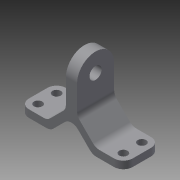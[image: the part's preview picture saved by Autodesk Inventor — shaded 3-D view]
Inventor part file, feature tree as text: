
AUTODESK INVENTOR PART (.ipt)
format: ipt  version: 2013 (Build 170138000, 138)  size: 150,016 bytes
history: native  units: mm
features: fillet x3, sketch x3, hole x2, extrude x1, mirror x1
ambient origin geometry x8: Origin, YZ Plane, XZ Plane, XY Plane, X Axis, Y Axis, Z Axis, Center Point
bodies: Solid1 (feature_tree)
feature tree (10):
  extrude  "Extrusion1"  TaperAngle=135.0deg  [1 undecoded]
  fillet  "Fillet1"  Radius=15.0mm
  hole  "Hole2"  [1 undecoded]
  hole  "Hole3"  [1 undecoded]
  fillet  "Fillet4"  Radius=5.0mm
  mirror  "Mirror2"
  fillet  "Fillet5"  Radius=10.0mm
  sketch  "Sketch1"  dims[d4=3.0mm d6=135.0deg d7=15.0mm]
  sketch  "Sketch3"  dims[d9=4.0mm d10=25.0mm]
  sketch  "Sketch4"  dims[d11=20.0mm d12=0.0mm d13=10.0mm d21=6.6mm d22=6.0mm d23=12.6mm d24=2.0mm d25=90.0deg d26=8.0mm d27=20.594885mm d28=5.0mm d29=10.0mm d30=4.5mm d31=6.0mm d32=9.4mm d33=2.0mm d34=90.0deg d35=8.0mm d36=20.594885mm d38=10.0mm d39=4.0mm d40=5.0mm d42=5.0mm d43=5.0mm]
note: 3 required parameter values undecoded (feature->parameter linkage not recoverable at this tier; creation-order binding heuristic only, values carry confidence <= 0.55)
